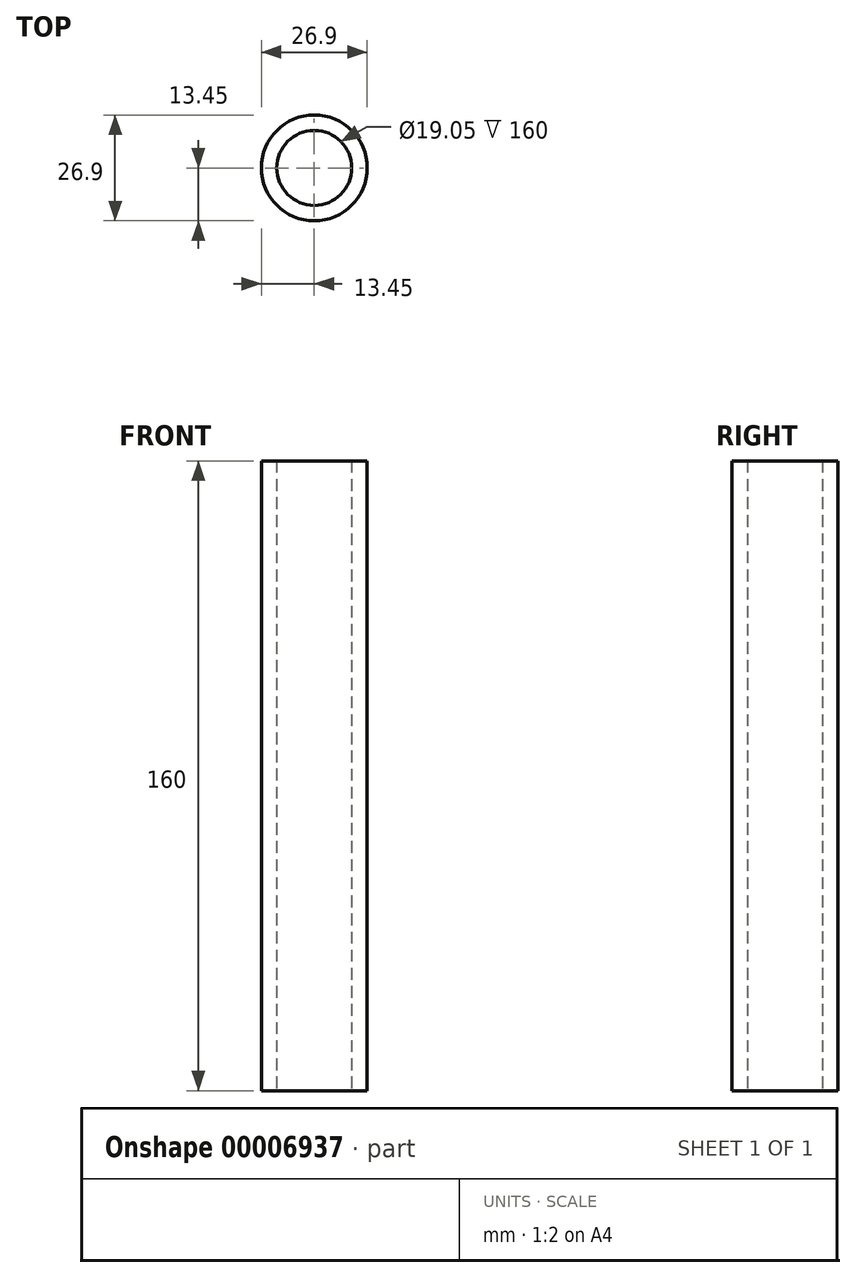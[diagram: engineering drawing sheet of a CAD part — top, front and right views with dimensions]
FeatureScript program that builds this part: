
annotation { "Feature Type Name" : "Feature", "Feature Type Description" : "" }
export const myFeature = defineFeature(function(context is Context, id is Id, definition is map)
    precondition{}
    {
        {
            var Q0;
            Q0=qCreatedBy(makeId("Top.planeOp"),FACE);
            var sketch = newSketch(context, id + "F0", { "sketchPlane" : qUnion([Q0])});
            skCircle(sketch, "E0", {"center": v(0, 0) * mm, "radius": 13.45 * mm});
            skCircle(sketch, "E1", {"center": v(0, 0) * mm, "radius": 9.53 * mm});
            skSolve(sketch);
        }
        {
            var Q0;
            Q0=makeQuery(id+"F0.imprint","IMPRINT",FACE,{"disambiguationData":[TD([[makeQuery(id+"F0.imprint","IMPRINT",EDGE,{"derivedFrom":sQuery(id+"F0.wireOp",EDGE,"E0")}),1.0]])]});
            extrude(context, id + "F1", {"entities" : qUnion([Q0]), "depth" : (160) * mm});
        }
    });
